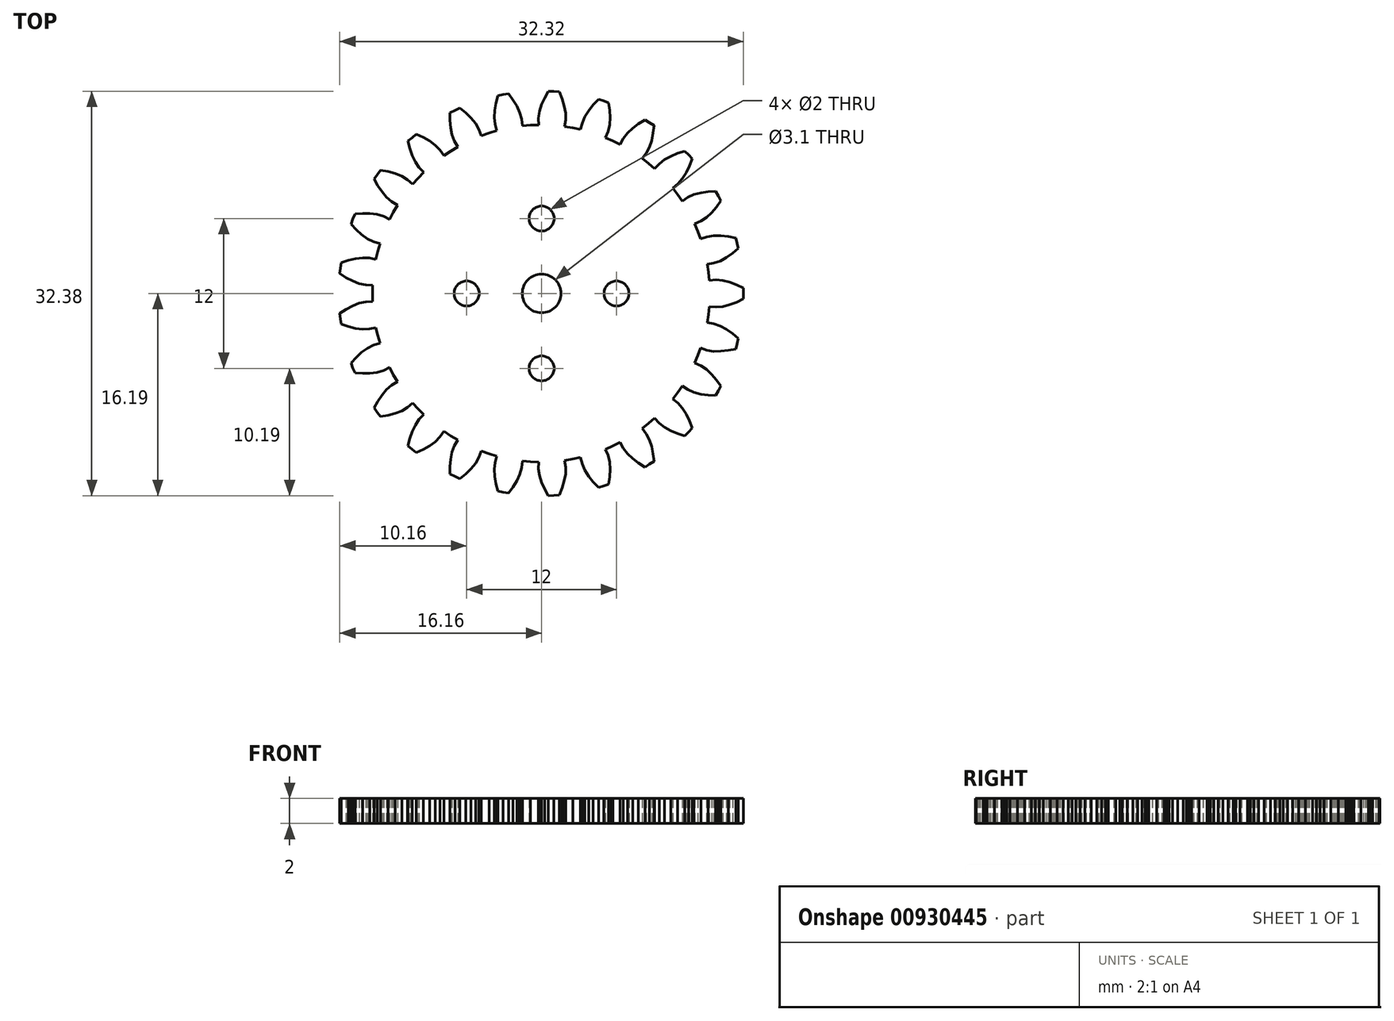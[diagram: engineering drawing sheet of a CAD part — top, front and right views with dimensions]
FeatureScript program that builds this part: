
annotation { "Feature Type Name" : "Feature", "Feature Type Description" : "" }
export const myFeature = defineFeature(function(context is Context, id is Id, definition is map)
    precondition{}
    {
        {
            var Q0;
            Q0=qCreatedBy(makeId("Top.planeOp"),FACE);
            var sketch = newSketch(context, id + "F0", { "sketchPlane" : qUnion([Q0])});
            skLineSegment(sketch, "E0", {"start": v(13.35, -1.7) * mm, "end": v(13.42, -1.05) * mm});
            skLineSegment(sketch, "E1", {"start": v(13.42, -1.05) * mm, "end": v(13.96, -1.1) * mm});
            skLineSegment(sketch, "E2", {"start": v(13.96, -1.1) * mm, "end": v(14.5, -1.05) * mm});
            skLineSegment(sketch, "E3", {"start": v(14.5, -1.05) * mm, "end": v(15.05, -0.9) * mm});
            skLineSegment(sketch, "E4", {"start": v(15.05, -0.9) * mm, "end": v(15.6, -0.7) * mm});
            skLineSegment(sketch, "E5", {"start": v(15.6, -0.7) * mm, "end": v(16.15, -0.43) * mm});
            skLineSegment(sketch, "E6", {"start": v(16.15, -0.43) * mm, "end": v(16.16, 0) * mm});
            skLineSegment(sketch, "E7", {"start": v(16.16, 0) * mm, "end": v(16.15, 0.43) * mm});
            skLineSegment(sketch, "E8", {"start": v(16.15, 0.43) * mm, "end": v(15.6, 0.7) * mm});
            skLineSegment(sketch, "E9", {"start": v(15.6, 0.7) * mm, "end": v(15.05, 0.9) * mm});
            skLineSegment(sketch, "E10", {"start": v(15.05, 0.9) * mm, "end": v(14.5, 1.05) * mm});
            skLineSegment(sketch, "E11", {"start": v(14.5, 1.05) * mm, "end": v(13.96, 1.1) * mm});
            skLineSegment(sketch, "E12", {"start": v(13.96, 1.1) * mm, "end": v(13.42, 1.05) * mm});
            skLineSegment(sketch, "E13", {"start": v(13.42, 1.05) * mm, "end": v(13.35, 1.7) * mm});
            skLineSegment(sketch, "E14", {"start": v(13.35, 1.7) * mm, "end": v(13.26, 2.33) * mm});
            skLineSegment(sketch, "E15", {"start": v(13.26, 2.33) * mm, "end": v(13.79, 2.42) * mm});
            skLineSegment(sketch, "E16", {"start": v(13.79, 2.42) * mm, "end": v(14.3, 2.6) * mm});
            skLineSegment(sketch, "E17", {"start": v(14.3, 2.6) * mm, "end": v(14.8, 2.88) * mm});
            skLineSegment(sketch, "E18", {"start": v(14.8, 2.88) * mm, "end": v(15.29, 3.22) * mm});
            skLineSegment(sketch, "E19", {"start": v(15.29, 3.22) * mm, "end": v(15.75, 3.6) * mm});
            skLineSegment(sketch, "E20", {"start": v(15.75, 3.6) * mm, "end": v(15.65, 4.03) * mm});
            skLineSegment(sketch, "E21", {"start": v(15.65, 4.03) * mm, "end": v(15.54, 4.45) * mm});
            skLineSegment(sketch, "E22", {"start": v(15.54, 4.45) * mm, "end": v(14.94, 4.57) * mm});
            skLineSegment(sketch, "E23", {"start": v(14.94, 4.57) * mm, "end": v(14.35, 4.63) * mm});
            skLineSegment(sketch, "E24", {"start": v(14.35, 4.63) * mm, "end": v(13.79, 4.63) * mm});
            skLineSegment(sketch, "E25", {"start": v(13.79, 4.63) * mm, "end": v(13.25, 4.54) * mm});
            skLineSegment(sketch, "E26", {"start": v(13.25, 4.54) * mm, "end": v(12.74, 4.36) * mm});
            skLineSegment(sketch, "E27", {"start": v(12.74, 4.36) * mm, "end": v(12.51, 4.97) * mm});
            skLineSegment(sketch, "E28", {"start": v(12.51, 4.97) * mm, "end": v(12.26, 5.57) * mm});
            skLineSegment(sketch, "E29", {"start": v(12.26, 5.57) * mm, "end": v(12.75, 5.79) * mm});
            skLineSegment(sketch, "E30", {"start": v(12.75, 5.79) * mm, "end": v(13.2, 6.09) * mm});
            skLineSegment(sketch, "E31", {"start": v(13.2, 6.09) * mm, "end": v(13.62, 6.48) * mm});
            skLineSegment(sketch, "E32", {"start": v(13.62, 6.48) * mm, "end": v(14, 6.93) * mm});
            skLineSegment(sketch, "E33", {"start": v(14, 6.93) * mm, "end": v(14.36, 7.42) * mm});
            skLineSegment(sketch, "E34", {"start": v(14.36, 7.42) * mm, "end": v(14.16, 7.8) * mm});
            skLineSegment(sketch, "E35", {"start": v(14.16, 7.8) * mm, "end": v(13.94, 8.18) * mm});
            skLineSegment(sketch, "E36", {"start": v(13.94, 8.18) * mm, "end": v(13.33, 8.15) * mm});
            skLineSegment(sketch, "E37", {"start": v(13.33, 8.15) * mm, "end": v(12.75, 8.06) * mm});
            skLineSegment(sketch, "E38", {"start": v(12.75, 8.06) * mm, "end": v(12.2, 7.92) * mm});
            skLineSegment(sketch, "E39", {"start": v(12.2, 7.92) * mm, "end": v(11.7, 7.7) * mm});
            skLineSegment(sketch, "E40", {"start": v(11.7, 7.7) * mm, "end": v(11.25, 7.4) * mm});
            skLineSegment(sketch, "E41", {"start": v(11.25, 7.4) * mm, "end": v(10.88, 7.94) * mm});
            skLineSegment(sketch, "E42", {"start": v(10.88, 7.94) * mm, "end": v(10.49, 8.45) * mm});
            skLineSegment(sketch, "E43", {"start": v(10.49, 8.45) * mm, "end": v(10.91, 8.79) * mm});
            skLineSegment(sketch, "E44", {"start": v(10.91, 8.79) * mm, "end": v(11.28, 9.2) * mm});
            skLineSegment(sketch, "E45", {"start": v(11.28, 9.2) * mm, "end": v(11.58, 9.67) * mm});
            skLineSegment(sketch, "E46", {"start": v(11.58, 9.67) * mm, "end": v(11.84, 10.2) * mm});
            skLineSegment(sketch, "E47", {"start": v(11.84, 10.2) * mm, "end": v(12.06, 10.77) * mm});
            skLineSegment(sketch, "E48", {"start": v(12.06, 10.77) * mm, "end": v(11.77, 11.09) * mm});
            skLineSegment(sketch, "E49", {"start": v(11.77, 11.09) * mm, "end": v(11.47, 11.4) * mm});
            skLineSegment(sketch, "E50", {"start": v(11.47, 11.4) * mm, "end": v(10.89, 11.22) * mm});
            skLineSegment(sketch, "E51", {"start": v(10.89, 11.22) * mm, "end": v(10.34, 11) * mm});
            skLineSegment(sketch, "E52", {"start": v(10.34, 11) * mm, "end": v(9.85, 10.72) * mm});
            skLineSegment(sketch, "E53", {"start": v(9.85, 10.72) * mm, "end": v(9.42, 10.38) * mm});
            skLineSegment(sketch, "E54", {"start": v(9.42, 10.38) * mm, "end": v(9.05, 9.98) * mm});
            skLineSegment(sketch, "E55", {"start": v(9.05, 9.98) * mm, "end": v(8.57, 10.4) * mm});
            skLineSegment(sketch, "E56", {"start": v(8.57, 10.4) * mm, "end": v(8.06, 10.8) * mm});
            skLineSegment(sketch, "E57", {"start": v(8.06, 10.8) * mm, "end": v(8.38, 11.23) * mm});
            skLineSegment(sketch, "E58", {"start": v(8.38, 11.23) * mm, "end": v(8.64, 11.72) * mm});
            skLineSegment(sketch, "E59", {"start": v(8.64, 11.72) * mm, "end": v(8.81, 12.26) * mm});
            skLineSegment(sketch, "E60", {"start": v(8.81, 12.26) * mm, "end": v(8.93, 12.84) * mm});
            skLineSegment(sketch, "E61", {"start": v(8.93, 12.84) * mm, "end": v(9, 13.44) * mm});
            skLineSegment(sketch, "E62", {"start": v(9, 13.44) * mm, "end": v(8.64, 13.68) * mm});
            skLineSegment(sketch, "E63", {"start": v(8.64, 13.68) * mm, "end": v(8.27, 13.9) * mm});
            skLineSegment(sketch, "E64", {"start": v(8.27, 13.9) * mm, "end": v(7.76, 13.58) * mm});
            skLineSegment(sketch, "E65", {"start": v(7.76, 13.58) * mm, "end": v(7.28, 13.23) * mm});
            skLineSegment(sketch, "E66", {"start": v(7.28, 13.23) * mm, "end": v(6.87, 12.84) * mm});
            skLineSegment(sketch, "E67", {"start": v(6.87, 12.84) * mm, "end": v(6.54, 12.4) * mm});
            skLineSegment(sketch, "E68", {"start": v(6.54, 12.4) * mm, "end": v(6.29, 11.93) * mm});
            skLineSegment(sketch, "E69", {"start": v(6.29, 11.93) * mm, "end": v(5.7, 12.22) * mm});
            skLineSegment(sketch, "E70", {"start": v(5.7, 12.22) * mm, "end": v(5.12, 12.48) * mm});
            skLineSegment(sketch, "E71", {"start": v(5.12, 12.48) * mm, "end": v(5.32, 12.98) * mm});
            skLineSegment(sketch, "E72", {"start": v(5.32, 12.98) * mm, "end": v(5.45, 13.5) * mm});
            skLineSegment(sketch, "E73", {"start": v(5.45, 13.5) * mm, "end": v(5.48, 14.07) * mm});
            skLineSegment(sketch, "E74", {"start": v(5.48, 14.07) * mm, "end": v(5.46, 14.66) * mm});
            skLineSegment(sketch, "E75", {"start": v(5.46, 14.66) * mm, "end": v(5.38, 15.27) * mm});
            skLineSegment(sketch, "E76", {"start": v(5.38, 15.27) * mm, "end": v(4.97, 15.4) * mm});
            skLineSegment(sketch, "E77", {"start": v(4.97, 15.4) * mm, "end": v(4.55, 15.54) * mm});
            skLineSegment(sketch, "E78", {"start": v(4.55, 15.54) * mm, "end": v(4.13, 15.1) * mm});
            skLineSegment(sketch, "E79", {"start": v(4.13, 15.1) * mm, "end": v(3.76, 14.63) * mm});
            skLineSegment(sketch, "E80", {"start": v(3.76, 14.63) * mm, "end": v(3.46, 14.15) * mm});
            skLineSegment(sketch, "E81", {"start": v(3.46, 14.15) * mm, "end": v(3.25, 13.65) * mm});
            skLineSegment(sketch, "E82", {"start": v(3.25, 13.65) * mm, "end": v(3.12, 13.12) * mm});
            skLineSegment(sketch, "E83", {"start": v(3.12, 13.12) * mm, "end": v(2.49, 13.26) * mm});
            skLineSegment(sketch, "E84", {"start": v(2.49, 13.26) * mm, "end": v(1.85, 13.37) * mm});
            skLineSegment(sketch, "E85", {"start": v(1.85, 13.37) * mm, "end": v(1.93, 13.9) * mm});
            skLineSegment(sketch, "E86", {"start": v(1.93, 13.9) * mm, "end": v(1.92, 14.45) * mm});
            skLineSegment(sketch, "E87", {"start": v(1.92, 14.45) * mm, "end": v(1.81, 15) * mm});
            skLineSegment(sketch, "E88", {"start": v(1.81, 15) * mm, "end": v(1.64, 15.57) * mm});
            skLineSegment(sketch, "E89", {"start": v(1.64, 15.57) * mm, "end": v(1.4, 16.14) * mm});
            skLineSegment(sketch, "E90", {"start": v(1.4, 16.14) * mm, "end": v(0.98, 16.17) * mm});
            skLineSegment(sketch, "E91", {"start": v(0.98, 16.17) * mm, "end": v(0.55, 16.19) * mm});
            skLineSegment(sketch, "E92", {"start": v(0.55, 16.19) * mm, "end": v(0.25, 15.66) * mm});
            skLineSegment(sketch, "E93", {"start": v(0.25, 15.66) * mm, "end": v(0, 15.12) * mm});
            skLineSegment(sketch, "E94", {"start": v(0, 15.12) * mm, "end": v(-0.17, 14.58) * mm});
            skLineSegment(sketch, "E95", {"start": v(-0.17, 14.58) * mm, "end": v(-0.25, 14.04) * mm});
            skLineSegment(sketch, "E96", {"start": v(-0.25, 14.04) * mm, "end": v(-0.24, 13.5) * mm});
            skLineSegment(sketch, "E97", {"start": v(-0.24, 13.5) * mm, "end": v(-0.89, 13.47) * mm});
            skLineSegment(sketch, "E98", {"start": v(-0.89, 13.47) * mm, "end": v(-1.53, 13.42) * mm});
            skLineSegment(sketch, "E99", {"start": v(-1.53, 13.42) * mm, "end": v(-1.6, 13.95) * mm});
            skLineSegment(sketch, "E100", {"start": v(-1.6, 13.95) * mm, "end": v(-1.74, 14.48) * mm});
            skLineSegment(sketch, "E101", {"start": v(-1.74, 14.48) * mm, "end": v(-1.98, 15) * mm});
            skLineSegment(sketch, "E102", {"start": v(-1.98, 15) * mm, "end": v(-2.29, 15.5) * mm});
            skLineSegment(sketch, "E103", {"start": v(-2.29, 15.5) * mm, "end": v(-2.65, 15.99) * mm});
            skLineSegment(sketch, "E104", {"start": v(-2.65, 15.99) * mm, "end": v(-3.08, 15.91) * mm});
            skLineSegment(sketch, "E105", {"start": v(-3.08, 15.91) * mm, "end": v(-3.5, 15.83) * mm});
            skLineSegment(sketch, "E106", {"start": v(-3.5, 15.83) * mm, "end": v(-3.66, 15.24) * mm});
            skLineSegment(sketch, "E107", {"start": v(-3.66, 15.24) * mm, "end": v(-3.76, 14.66) * mm});
            skLineSegment(sketch, "E108", {"start": v(-3.76, 14.66) * mm, "end": v(-3.8, 14.09) * mm});
            skLineSegment(sketch, "E109", {"start": v(-3.8, 14.09) * mm, "end": v(-3.73, 13.55) * mm});
            skLineSegment(sketch, "E110", {"start": v(-3.73, 13.55) * mm, "end": v(-3.6, 13.02) * mm});
            skLineSegment(sketch, "E111", {"start": v(-3.6, 13.02) * mm, "end": v(-4.21, 12.84) * mm});
            skLineSegment(sketch, "E112", {"start": v(-4.21, 12.84) * mm, "end": v(-4.82, 12.62) * mm});
            skLineSegment(sketch, "E113", {"start": v(-4.82, 12.62) * mm, "end": v(-5.01, 13.13) * mm});
            skLineSegment(sketch, "E114", {"start": v(-5.01, 13.13) * mm, "end": v(-5.28, 13.6) * mm});
            skLineSegment(sketch, "E115", {"start": v(-5.28, 13.6) * mm, "end": v(-5.65, 14.04) * mm});
            skLineSegment(sketch, "E116", {"start": v(-5.65, 14.04) * mm, "end": v(-6.07, 14.45) * mm});
            skLineSegment(sketch, "E117", {"start": v(-6.07, 14.45) * mm, "end": v(-6.54, 14.84) * mm});
            skLineSegment(sketch, "E118", {"start": v(-6.54, 14.84) * mm, "end": v(-6.94, 14.66) * mm});
            skLineSegment(sketch, "E119", {"start": v(-6.94, 14.66) * mm, "end": v(-7.33, 14.47) * mm});
            skLineSegment(sketch, "E120", {"start": v(-7.33, 14.47) * mm, "end": v(-7.33, 13.86) * mm});
            skLineSegment(sketch, "E121", {"start": v(-7.33, 13.86) * mm, "end": v(-7.28, 13.27) * mm});
            skLineSegment(sketch, "E122", {"start": v(-7.28, 13.27) * mm, "end": v(-7.18, 12.71) * mm});
            skLineSegment(sketch, "E123", {"start": v(-7.18, 12.71) * mm, "end": v(-6.99, 12.2) * mm});
            skLineSegment(sketch, "E124", {"start": v(-6.99, 12.2) * mm, "end": v(-6.72, 11.73) * mm});
            skLineSegment(sketch, "E125", {"start": v(-6.72, 11.73) * mm, "end": v(-7.27, 11.4) * mm});
            skLineSegment(sketch, "E126", {"start": v(-7.27, 11.4) * mm, "end": v(-7.81, 11.04) * mm});
            skLineSegment(sketch, "E127", {"start": v(-7.81, 11.04) * mm, "end": v(-8.12, 11.48) * mm});
            skLineSegment(sketch, "E128", {"start": v(-8.12, 11.48) * mm, "end": v(-8.5, 11.87) * mm});
            skLineSegment(sketch, "E129", {"start": v(-8.5, 11.87) * mm, "end": v(-8.96, 12.2) * mm});
            skLineSegment(sketch, "E130", {"start": v(-8.96, 12.2) * mm, "end": v(-9.48, 12.5) * mm});
            skLineSegment(sketch, "E131", {"start": v(-9.48, 12.5) * mm, "end": v(-10.03, 12.75) * mm});
            skLineSegment(sketch, "E132", {"start": v(-10.03, 12.75) * mm, "end": v(-10.37, 12.48) * mm});
            skLineSegment(sketch, "E133", {"start": v(-10.37, 12.48) * mm, "end": v(-10.7, 12.2) * mm});
            skLineSegment(sketch, "E134", {"start": v(-10.7, 12.2) * mm, "end": v(-10.55, 11.61) * mm});
            skLineSegment(sketch, "E135", {"start": v(-10.55, 11.61) * mm, "end": v(-10.36, 11.05) * mm});
            skLineSegment(sketch, "E136", {"start": v(-10.36, 11.05) * mm, "end": v(-10.12, 10.54) * mm});
            skLineSegment(sketch, "E137", {"start": v(-10.12, 10.54) * mm, "end": v(-9.8, 10.1) * mm});
            skLineSegment(sketch, "E138", {"start": v(-9.8, 10.1) * mm, "end": v(-9.43, 9.7) * mm});
            skLineSegment(sketch, "E139", {"start": v(-9.43, 9.7) * mm, "end": v(-9.88, 9.24) * mm});
            skLineSegment(sketch, "E140", {"start": v(-9.88, 9.24) * mm, "end": v(-10.31, 8.76) * mm});
            skLineSegment(sketch, "E141", {"start": v(-10.31, 8.76) * mm, "end": v(-10.72, 9.1) * mm});
            skLineSegment(sketch, "E142", {"start": v(-10.72, 9.1) * mm, "end": v(-11.19, 9.4) * mm});
            skLineSegment(sketch, "E143", {"start": v(-11.19, 9.4) * mm, "end": v(-11.72, 9.6) * mm});
            skLineSegment(sketch, "E144", {"start": v(-11.72, 9.6) * mm, "end": v(-12.29, 9.76) * mm});
            skLineSegment(sketch, "E145", {"start": v(-12.29, 9.76) * mm, "end": v(-12.89, 9.87) * mm});
            skLineSegment(sketch, "E146", {"start": v(-12.89, 9.87) * mm, "end": v(-13.15, 9.52) * mm});
            skLineSegment(sketch, "E147", {"start": v(-13.15, 9.52) * mm, "end": v(-13.4, 9.17) * mm});
            skLineSegment(sketch, "E148", {"start": v(-13.4, 9.17) * mm, "end": v(-13.1, 8.63) * mm});
            skLineSegment(sketch, "E149", {"start": v(-13.1, 8.63) * mm, "end": v(-12.78, 8.14) * mm});
            skLineSegment(sketch, "E150", {"start": v(-12.78, 8.14) * mm, "end": v(-12.42, 7.7) * mm});
            skLineSegment(sketch, "E151", {"start": v(-12.42, 7.7) * mm, "end": v(-12, 7.35) * mm});
            skLineSegment(sketch, "E152", {"start": v(-12, 7.35) * mm, "end": v(-11.54, 7.06) * mm});
            skLineSegment(sketch, "E153", {"start": v(-11.54, 7.06) * mm, "end": v(-11.87, 6.5) * mm});
            skLineSegment(sketch, "E154", {"start": v(-11.87, 6.5) * mm, "end": v(-12.17, 5.93) * mm});
            skLineSegment(sketch, "E155", {"start": v(-12.17, 5.93) * mm, "end": v(-12.65, 6.17) * mm});
            skLineSegment(sketch, "E156", {"start": v(-12.65, 6.17) * mm, "end": v(-13.18, 6.33) * mm});
            skLineSegment(sketch, "E157", {"start": v(-13.18, 6.33) * mm, "end": v(-13.74, 6.4) * mm});
            skLineSegment(sketch, "E158", {"start": v(-13.74, 6.4) * mm, "end": v(-14.33, 6.4) * mm});
            skLineSegment(sketch, "E159", {"start": v(-14.33, 6.4) * mm, "end": v(-14.94, 6.36) * mm});
            skLineSegment(sketch, "E160", {"start": v(-14.94, 6.36) * mm, "end": v(-15.1, 5.96) * mm});
            skLineSegment(sketch, "E161", {"start": v(-15.1, 5.96) * mm, "end": v(-15.26, 5.56) * mm});
            skLineSegment(sketch, "E162", {"start": v(-15.26, 5.56) * mm, "end": v(-14.84, 5.11) * mm});
            skLineSegment(sketch, "E163", {"start": v(-14.84, 5.11) * mm, "end": v(-14.4, 4.72) * mm});
            skLineSegment(sketch, "E164", {"start": v(-14.4, 4.72) * mm, "end": v(-13.95, 4.38) * mm});
            skLineSegment(sketch, "E165", {"start": v(-13.95, 4.38) * mm, "end": v(-13.46, 4.14) * mm});
            skLineSegment(sketch, "E166", {"start": v(-13.46, 4.14) * mm, "end": v(-12.94, 3.98) * mm});
            skLineSegment(sketch, "E167", {"start": v(-12.94, 3.98) * mm, "end": v(-13.12, 3.36) * mm});
            skLineSegment(sketch, "E168", {"start": v(-13.12, 3.36) * mm, "end": v(-13.26, 2.73) * mm});
            skLineSegment(sketch, "E169", {"start": v(-13.26, 2.73) * mm, "end": v(-13.8, 2.84) * mm});
            skLineSegment(sketch, "E170", {"start": v(-13.8, 2.84) * mm, "end": v(-14.34, 2.86) * mm});
            skLineSegment(sketch, "E171", {"start": v(-14.34, 2.86) * mm, "end": v(-14.9, 2.79) * mm});
            skLineSegment(sketch, "E172", {"start": v(-14.9, 2.79) * mm, "end": v(-15.47, 2.65) * mm});
            skLineSegment(sketch, "E173", {"start": v(-15.47, 2.65) * mm, "end": v(-16.05, 2.46) * mm});
            skLineSegment(sketch, "E174", {"start": v(-16.05, 2.46) * mm, "end": v(-16.11, 2.03) * mm});
            skLineSegment(sketch, "E175", {"start": v(-16.11, 2.03) * mm, "end": v(-16.16, 1.6) * mm});
            skLineSegment(sketch, "E176", {"start": v(-16.16, 1.6) * mm, "end": v(-15.65, 1.27) * mm});
            skLineSegment(sketch, "E177", {"start": v(-15.65, 1.27) * mm, "end": v(-15.13, 1) * mm});
            skLineSegment(sketch, "E178", {"start": v(-15.13, 1) * mm, "end": v(-14.6, 0.78) * mm});
            skLineSegment(sketch, "E179", {"start": v(-14.6, 0.78) * mm, "end": v(-14.06, 0.67) * mm});
            skLineSegment(sketch, "E180", {"start": v(-14.06, 0.67) * mm, "end": v(-13.52, 0.65) * mm});
            skLineSegment(sketch, "E181", {"start": v(-13.52, 0.65) * mm, "end": v(-13.54, 0) * mm});
            skLineSegment(sketch, "E182", {"start": v(-13.54, 0) * mm, "end": v(-13.52, -0.65) * mm});
            skLineSegment(sketch, "E183", {"start": v(-13.52, -0.65) * mm, "end": v(-14.06, -0.67) * mm});
            skLineSegment(sketch, "E184", {"start": v(-14.06, -0.67) * mm, "end": v(-14.6, -0.78) * mm});
            skLineSegment(sketch, "E185", {"start": v(-14.6, -0.78) * mm, "end": v(-15.13, -1) * mm});
            skLineSegment(sketch, "E186", {"start": v(-15.13, -1) * mm, "end": v(-15.65, -1.27) * mm});
            skLineSegment(sketch, "E187", {"start": v(-15.65, -1.27) * mm, "end": v(-16.16, -1.6) * mm});
            skLineSegment(sketch, "E188", {"start": v(-16.16, -1.6) * mm, "end": v(-16.11, -2.03) * mm});
            skLineSegment(sketch, "E189", {"start": v(-16.11, -2.03) * mm, "end": v(-16.05, -2.46) * mm});
            skLineSegment(sketch, "E190", {"start": v(-16.05, -2.46) * mm, "end": v(-15.47, -2.65) * mm});
            skLineSegment(sketch, "E191", {"start": v(-15.47, -2.65) * mm, "end": v(-14.9, -2.79) * mm});
            skLineSegment(sketch, "E192", {"start": v(-14.9, -2.79) * mm, "end": v(-14.34, -2.86) * mm});
            skLineSegment(sketch, "E193", {"start": v(-14.34, -2.86) * mm, "end": v(-13.8, -2.84) * mm});
            skLineSegment(sketch, "E194", {"start": v(-13.8, -2.84) * mm, "end": v(-13.26, -2.73) * mm});
            skLineSegment(sketch, "E195", {"start": v(-13.26, -2.73) * mm, "end": v(-13.12, -3.36) * mm});
            skLineSegment(sketch, "E196", {"start": v(-13.12, -3.36) * mm, "end": v(-12.94, -3.98) * mm});
            skLineSegment(sketch, "E197", {"start": v(-12.94, -3.98) * mm, "end": v(-13.46, -4.14) * mm});
            skLineSegment(sketch, "E198", {"start": v(-13.46, -4.14) * mm, "end": v(-13.95, -4.38) * mm});
            skLineSegment(sketch, "E199", {"start": v(-13.95, -4.38) * mm, "end": v(-14.4, -4.72) * mm});
            skLineSegment(sketch, "E200", {"start": v(-14.4, -4.72) * mm, "end": v(-14.84, -5.11) * mm});
            skLineSegment(sketch, "E201", {"start": v(-14.84, -5.11) * mm, "end": v(-15.26, -5.56) * mm});
            skLineSegment(sketch, "E202", {"start": v(-15.26, -5.56) * mm, "end": v(-15.1, -5.96) * mm});
            skLineSegment(sketch, "E203", {"start": v(-15.1, -5.96) * mm, "end": v(-14.94, -6.36) * mm});
            skLineSegment(sketch, "E204", {"start": v(-14.94, -6.36) * mm, "end": v(-14.33, -6.4) * mm});
            skLineSegment(sketch, "E205", {"start": v(-14.33, -6.4) * mm, "end": v(-13.74, -6.4) * mm});
            skLineSegment(sketch, "E206", {"start": v(-13.74, -6.4) * mm, "end": v(-13.18, -6.33) * mm});
            skLineSegment(sketch, "E207", {"start": v(-13.18, -6.33) * mm, "end": v(-12.65, -6.17) * mm});
            skLineSegment(sketch, "E208", {"start": v(-12.65, -6.17) * mm, "end": v(-12.17, -5.93) * mm});
            skLineSegment(sketch, "E209", {"start": v(-12.17, -5.93) * mm, "end": v(-11.87, -6.5) * mm});
            skLineSegment(sketch, "E210", {"start": v(-11.87, -6.5) * mm, "end": v(-11.54, -7.06) * mm});
            skLineSegment(sketch, "E211", {"start": v(-11.54, -7.06) * mm, "end": v(-12, -7.35) * mm});
            skLineSegment(sketch, "E212", {"start": v(-12, -7.35) * mm, "end": v(-12.42, -7.7) * mm});
            skLineSegment(sketch, "E213", {"start": v(-12.42, -7.7) * mm, "end": v(-12.78, -8.14) * mm});
            skLineSegment(sketch, "E214", {"start": v(-12.78, -8.14) * mm, "end": v(-13.1, -8.63) * mm});
            skLineSegment(sketch, "E215", {"start": v(-13.1, -8.63) * mm, "end": v(-13.4, -9.17) * mm});
            skLineSegment(sketch, "E216", {"start": v(-13.4, -9.17) * mm, "end": v(-13.15, -9.52) * mm});
            skLineSegment(sketch, "E217", {"start": v(-13.15, -9.52) * mm, "end": v(-12.89, -9.87) * mm});
            skLineSegment(sketch, "E218", {"start": v(-12.89, -9.87) * mm, "end": v(-12.29, -9.76) * mm});
            skLineSegment(sketch, "E219", {"start": v(-12.29, -9.76) * mm, "end": v(-11.72, -9.6) * mm});
            skLineSegment(sketch, "E220", {"start": v(-11.72, -9.6) * mm, "end": v(-11.19, -9.4) * mm});
            skLineSegment(sketch, "E221", {"start": v(-11.19, -9.4) * mm, "end": v(-10.72, -9.1) * mm});
            skLineSegment(sketch, "E222", {"start": v(-10.72, -9.1) * mm, "end": v(-10.31, -8.76) * mm});
            skLineSegment(sketch, "E223", {"start": v(-10.31, -8.76) * mm, "end": v(-9.88, -9.24) * mm});
            skLineSegment(sketch, "E224", {"start": v(-9.88, -9.24) * mm, "end": v(-9.43, -9.7) * mm});
            skLineSegment(sketch, "E225", {"start": v(-9.43, -9.7) * mm, "end": v(-9.8, -10.1) * mm});
            skLineSegment(sketch, "E226", {"start": v(-9.8, -10.1) * mm, "end": v(-10.12, -10.54) * mm});
            skLineSegment(sketch, "E227", {"start": v(-10.12, -10.54) * mm, "end": v(-10.36, -11.05) * mm});
            skLineSegment(sketch, "E228", {"start": v(-10.36, -11.05) * mm, "end": v(-10.55, -11.61) * mm});
            skLineSegment(sketch, "E229", {"start": v(-10.55, -11.61) * mm, "end": v(-10.7, -12.2) * mm});
            skLineSegment(sketch, "E230", {"start": v(-10.7, -12.2) * mm, "end": v(-10.37, -12.48) * mm});
            skLineSegment(sketch, "E231", {"start": v(-10.37, -12.48) * mm, "end": v(-10.03, -12.75) * mm});
            skLineSegment(sketch, "E232", {"start": v(-10.03, -12.75) * mm, "end": v(-9.48, -12.5) * mm});
            skLineSegment(sketch, "E233", {"start": v(-9.48, -12.5) * mm, "end": v(-8.96, -12.2) * mm});
            skLineSegment(sketch, "E234", {"start": v(-8.96, -12.2) * mm, "end": v(-8.5, -11.87) * mm});
            skLineSegment(sketch, "E235", {"start": v(-8.5, -11.87) * mm, "end": v(-8.12, -11.48) * mm});
            skLineSegment(sketch, "E236", {"start": v(-8.12, -11.48) * mm, "end": v(-7.81, -11.04) * mm});
            skLineSegment(sketch, "E237", {"start": v(-7.81, -11.04) * mm, "end": v(-7.27, -11.4) * mm});
            skLineSegment(sketch, "E238", {"start": v(-7.27, -11.4) * mm, "end": v(-6.72, -11.73) * mm});
            skLineSegment(sketch, "E239", {"start": v(-6.72, -11.73) * mm, "end": v(-6.99, -12.2) * mm});
            skLineSegment(sketch, "E240", {"start": v(-6.99, -12.2) * mm, "end": v(-7.18, -12.71) * mm});
            skLineSegment(sketch, "E241", {"start": v(-7.18, -12.71) * mm, "end": v(-7.28, -13.27) * mm});
            skLineSegment(sketch, "E242", {"start": v(-7.28, -13.27) * mm, "end": v(-7.33, -13.86) * mm});
            skLineSegment(sketch, "E243", {"start": v(-7.33, -13.86) * mm, "end": v(-7.33, -14.47) * mm});
            skLineSegment(sketch, "E244", {"start": v(-7.33, -14.47) * mm, "end": v(-6.94, -14.66) * mm});
            skLineSegment(sketch, "E245", {"start": v(-6.94, -14.66) * mm, "end": v(-6.54, -14.84) * mm});
            skLineSegment(sketch, "E246", {"start": v(-6.54, -14.84) * mm, "end": v(-6.07, -14.45) * mm});
            skLineSegment(sketch, "E247", {"start": v(-6.07, -14.45) * mm, "end": v(-5.65, -14.04) * mm});
            skLineSegment(sketch, "E248", {"start": v(-5.65, -14.04) * mm, "end": v(-5.28, -13.6) * mm});
            skLineSegment(sketch, "E249", {"start": v(-5.28, -13.6) * mm, "end": v(-5.01, -13.13) * mm});
            skLineSegment(sketch, "E250", {"start": v(-5.01, -13.13) * mm, "end": v(-4.82, -12.62) * mm});
            skLineSegment(sketch, "E251", {"start": v(-4.82, -12.62) * mm, "end": v(-4.21, -12.84) * mm});
            skLineSegment(sketch, "E252", {"start": v(-4.21, -12.84) * mm, "end": v(-3.6, -13.02) * mm});
            skLineSegment(sketch, "E253", {"start": v(-3.6, -13.02) * mm, "end": v(-3.73, -13.55) * mm});
            skLineSegment(sketch, "E254", {"start": v(-3.73, -13.55) * mm, "end": v(-3.8, -14.09) * mm});
            skLineSegment(sketch, "E255", {"start": v(-3.8, -14.09) * mm, "end": v(-3.76, -14.66) * mm});
            skLineSegment(sketch, "E256", {"start": v(-3.76, -14.66) * mm, "end": v(-3.66, -15.24) * mm});
            skLineSegment(sketch, "E257", {"start": v(-3.66, -15.24) * mm, "end": v(-3.5, -15.83) * mm});
            skLineSegment(sketch, "E258", {"start": v(-3.5, -15.83) * mm, "end": v(-3.08, -15.91) * mm});
            skLineSegment(sketch, "E259", {"start": v(-3.08, -15.91) * mm, "end": v(-2.65, -15.99) * mm});
            skLineSegment(sketch, "E260", {"start": v(-2.65, -15.99) * mm, "end": v(-2.29, -15.5) * mm});
            skLineSegment(sketch, "E261", {"start": v(-2.29, -15.5) * mm, "end": v(-1.98, -15) * mm});
            skLineSegment(sketch, "E262", {"start": v(-1.98, -15) * mm, "end": v(-1.74, -14.48) * mm});
            skLineSegment(sketch, "E263", {"start": v(-1.74, -14.48) * mm, "end": v(-1.6, -13.95) * mm});
            skLineSegment(sketch, "E264", {"start": v(-1.6, -13.95) * mm, "end": v(-1.53, -13.42) * mm});
            skLineSegment(sketch, "E265", {"start": v(-1.53, -13.42) * mm, "end": v(-0.89, -13.47) * mm});
            skLineSegment(sketch, "E266", {"start": v(-0.89, -13.47) * mm, "end": v(-0.24, -13.5) * mm});
            skLineSegment(sketch, "E267", {"start": v(-0.24, -13.5) * mm, "end": v(-0.25, -14.04) * mm});
            skLineSegment(sketch, "E268", {"start": v(-0.25, -14.04) * mm, "end": v(-0.17, -14.58) * mm});
            skLineSegment(sketch, "E269", {"start": v(-0.17, -14.58) * mm, "end": v(0, -15.12) * mm});
            skLineSegment(sketch, "E270", {"start": v(0, -15.12) * mm, "end": v(0.25, -15.66) * mm});
            skLineSegment(sketch, "E271", {"start": v(0.25, -15.66) * mm, "end": v(0.55, -16.19) * mm});
            skLineSegment(sketch, "E272", {"start": v(0.55, -16.19) * mm, "end": v(0.98, -16.17) * mm});
            skLineSegment(sketch, "E273", {"start": v(0.98, -16.17) * mm, "end": v(1.4, -16.14) * mm});
            skLineSegment(sketch, "E274", {"start": v(1.4, -16.14) * mm, "end": v(1.64, -15.57) * mm});
            skLineSegment(sketch, "E275", {"start": v(1.64, -15.57) * mm, "end": v(1.81, -15) * mm});
            skLineSegment(sketch, "E276", {"start": v(1.81, -15) * mm, "end": v(1.92, -14.45) * mm});
            skLineSegment(sketch, "E277", {"start": v(1.92, -14.45) * mm, "end": v(1.93, -13.9) * mm});
            skLineSegment(sketch, "E278", {"start": v(1.93, -13.9) * mm, "end": v(1.85, -13.37) * mm});
            skLineSegment(sketch, "E279", {"start": v(1.85, -13.37) * mm, "end": v(2.49, -13.26) * mm});
            skLineSegment(sketch, "E280", {"start": v(2.49, -13.26) * mm, "end": v(3.12, -13.12) * mm});
            skLineSegment(sketch, "E281", {"start": v(3.12, -13.12) * mm, "end": v(3.25, -13.65) * mm});
            skLineSegment(sketch, "E282", {"start": v(3.25, -13.65) * mm, "end": v(3.46, -14.15) * mm});
            skLineSegment(sketch, "E283", {"start": v(3.46, -14.15) * mm, "end": v(3.76, -14.63) * mm});
            skLineSegment(sketch, "E284", {"start": v(3.76, -14.63) * mm, "end": v(4.13, -15.1) * mm});
            skLineSegment(sketch, "E285", {"start": v(4.13, -15.1) * mm, "end": v(4.55, -15.54) * mm});
            skLineSegment(sketch, "E286", {"start": v(4.55, -15.54) * mm, "end": v(4.97, -15.4) * mm});
            skLineSegment(sketch, "E287", {"start": v(4.97, -15.4) * mm, "end": v(5.38, -15.27) * mm});
            skLineSegment(sketch, "E288", {"start": v(5.38, -15.27) * mm, "end": v(5.46, -14.66) * mm});
            skLineSegment(sketch, "E289", {"start": v(5.46, -14.66) * mm, "end": v(5.48, -14.07) * mm});
            skLineSegment(sketch, "E290", {"start": v(5.48, -14.07) * mm, "end": v(5.45, -13.5) * mm});
            skLineSegment(sketch, "E291", {"start": v(5.45, -13.5) * mm, "end": v(5.32, -12.98) * mm});
            skLineSegment(sketch, "E292", {"start": v(5.32, -12.98) * mm, "end": v(5.12, -12.48) * mm});
            skLineSegment(sketch, "E293", {"start": v(5.12, -12.48) * mm, "end": v(5.7, -12.22) * mm});
            skLineSegment(sketch, "E294", {"start": v(5.7, -12.22) * mm, "end": v(6.29, -11.93) * mm});
            skLineSegment(sketch, "E295", {"start": v(6.29, -11.93) * mm, "end": v(6.54, -12.4) * mm});
            skLineSegment(sketch, "E296", {"start": v(6.54, -12.4) * mm, "end": v(6.87, -12.84) * mm});
            skLineSegment(sketch, "E297", {"start": v(6.87, -12.84) * mm, "end": v(7.28, -13.23) * mm});
            skLineSegment(sketch, "E298", {"start": v(7.28, -13.23) * mm, "end": v(7.76, -13.58) * mm});
            skLineSegment(sketch, "E299", {"start": v(7.76, -13.58) * mm, "end": v(8.27, -13.9) * mm});
            skLineSegment(sketch, "E300", {"start": v(8.27, -13.9) * mm, "end": v(8.64, -13.68) * mm});
            skLineSegment(sketch, "E301", {"start": v(8.64, -13.68) * mm, "end": v(9, -13.44) * mm});
            skLineSegment(sketch, "E302", {"start": v(9, -13.44) * mm, "end": v(8.93, -12.84) * mm});
            skLineSegment(sketch, "E303", {"start": v(8.93, -12.84) * mm, "end": v(8.81, -12.26) * mm});
            skLineSegment(sketch, "E304", {"start": v(8.81, -12.26) * mm, "end": v(8.64, -11.72) * mm});
            skLineSegment(sketch, "E305", {"start": v(8.64, -11.72) * mm, "end": v(8.38, -11.23) * mm});
            skLineSegment(sketch, "E306", {"start": v(8.38, -11.23) * mm, "end": v(8.06, -10.8) * mm});
            skLineSegment(sketch, "E307", {"start": v(8.06, -10.8) * mm, "end": v(8.57, -10.4) * mm});
            skLineSegment(sketch, "E308", {"start": v(8.57, -10.4) * mm, "end": v(9.05, -9.98) * mm});
            skLineSegment(sketch, "E309", {"start": v(9.05, -9.98) * mm, "end": v(9.42, -10.38) * mm});
            skLineSegment(sketch, "E310", {"start": v(9.42, -10.38) * mm, "end": v(9.85, -10.72) * mm});
            skLineSegment(sketch, "E311", {"start": v(9.85, -10.72) * mm, "end": v(10.34, -11) * mm});
            skLineSegment(sketch, "E312", {"start": v(10.34, -11) * mm, "end": v(10.89, -11.22) * mm});
            skLineSegment(sketch, "E313", {"start": v(10.89, -11.22) * mm, "end": v(11.47, -11.4) * mm});
            skLineSegment(sketch, "E314", {"start": v(11.47, -11.4) * mm, "end": v(11.77, -11.09) * mm});
            skLineSegment(sketch, "E315", {"start": v(11.77, -11.09) * mm, "end": v(12.06, -10.77) * mm});
            skLineSegment(sketch, "E316", {"start": v(12.06, -10.77) * mm, "end": v(11.84, -10.2) * mm});
            skLineSegment(sketch, "E317", {"start": v(11.84, -10.2) * mm, "end": v(11.58, -9.67) * mm});
            skLineSegment(sketch, "E318", {"start": v(11.58, -9.67) * mm, "end": v(11.28, -9.2) * mm});
            skLineSegment(sketch, "E319", {"start": v(11.28, -9.2) * mm, "end": v(10.91, -8.79) * mm});
            skLineSegment(sketch, "E320", {"start": v(10.91, -8.79) * mm, "end": v(10.49, -8.45) * mm});
            skLineSegment(sketch, "E321", {"start": v(10.49, -8.45) * mm, "end": v(10.88, -7.94) * mm});
            skLineSegment(sketch, "E322", {"start": v(10.88, -7.94) * mm, "end": v(11.25, -7.4) * mm});
            skLineSegment(sketch, "E323", {"start": v(11.25, -7.4) * mm, "end": v(11.7, -7.7) * mm});
            skLineSegment(sketch, "E324", {"start": v(11.7, -7.7) * mm, "end": v(12.2, -7.92) * mm});
            skLineSegment(sketch, "E325", {"start": v(12.2, -7.92) * mm, "end": v(12.75, -8.06) * mm});
            skLineSegment(sketch, "E326", {"start": v(12.75, -8.06) * mm, "end": v(13.33, -8.15) * mm});
            skLineSegment(sketch, "E327", {"start": v(13.33, -8.15) * mm, "end": v(13.94, -8.18) * mm});
            skLineSegment(sketch, "E328", {"start": v(13.94, -8.18) * mm, "end": v(14.16, -7.8) * mm});
            skLineSegment(sketch, "E329", {"start": v(14.16, -7.8) * mm, "end": v(14.36, -7.42) * mm});
            skLineSegment(sketch, "E330", {"start": v(14.36, -7.42) * mm, "end": v(14, -6.93) * mm});
            skLineSegment(sketch, "E331", {"start": v(14, -6.93) * mm, "end": v(13.62, -6.48) * mm});
            skLineSegment(sketch, "E332", {"start": v(13.62, -6.48) * mm, "end": v(13.2, -6.09) * mm});
            skLineSegment(sketch, "E333", {"start": v(13.2, -6.09) * mm, "end": v(12.75, -5.79) * mm});
            skLineSegment(sketch, "E334", {"start": v(12.75, -5.79) * mm, "end": v(12.26, -5.57) * mm});
            skLineSegment(sketch, "E335", {"start": v(12.26, -5.57) * mm, "end": v(12.51, -4.97) * mm});
            skLineSegment(sketch, "E336", {"start": v(12.51, -4.97) * mm, "end": v(12.74, -4.36) * mm});
            skLineSegment(sketch, "E337", {"start": v(12.74, -4.36) * mm, "end": v(13.25, -4.54) * mm});
            skLineSegment(sketch, "E338", {"start": v(13.25, -4.54) * mm, "end": v(13.79, -4.63) * mm});
            skLineSegment(sketch, "E339", {"start": v(13.79, -4.63) * mm, "end": v(14.35, -4.63) * mm});
            skLineSegment(sketch, "E340", {"start": v(14.35, -4.63) * mm, "end": v(14.94, -4.57) * mm});
            skLineSegment(sketch, "E341", {"start": v(14.94, -4.57) * mm, "end": v(15.54, -4.45) * mm});
            skLineSegment(sketch, "E342", {"start": v(15.54, -4.45) * mm, "end": v(15.65, -4.03) * mm});
            skLineSegment(sketch, "E343", {"start": v(15.65, -4.03) * mm, "end": v(15.75, -3.6) * mm});
            skLineSegment(sketch, "E344", {"start": v(15.75, -3.6) * mm, "end": v(15.29, -3.22) * mm});
            skLineSegment(sketch, "E345", {"start": v(15.29, -3.22) * mm, "end": v(14.8, -2.88) * mm});
            skLineSegment(sketch, "E346", {"start": v(14.8, -2.88) * mm, "end": v(14.3, -2.6) * mm});
            skLineSegment(sketch, "E347", {"start": v(14.3, -2.6) * mm, "end": v(13.79, -2.42) * mm});
            skLineSegment(sketch, "E348", {"start": v(13.79, -2.42) * mm, "end": v(13.26, -2.33) * mm});
            skLineSegment(sketch, "E349", {"start": v(13.35, -1.7) * mm, "end": v(13.26, -2.33) * mm});
            skSolve(sketch);
        }
        {
            var Q0;
            Q0=qCreatedBy(makeId("Top.planeOp"),FACE);
            cPlane(context, id + "F1", {"entities" : qUnion([Q0]), "cplaneType" : CPlaneType.OFFSET, "offset" : 25 * mm, "width" : 150 * mm, "height" : 150 * mm});
        }
        {
            var Q0;
            Q0=makeQuery(id+"F0.imprint","IMPRINT",FACE,{"disambiguationData":[TD([[makeQuery(id+"F0.imprint","IMPRINT",EDGE,{"derivedFrom":sQuery(id+"F0.wireOp",EDGE,"E0")}),1.0]])]});
            var sketch = newSketch(context, id + "F2", { "sketchPlane" : qUnion([Q0])});
            skCircle(sketch, "E350", {"center": v(0, 0) * mm, "radius": 1.55 * mm});
            skCircle(sketch, "E351", {"center": v(0, 6) * mm, "radius": 1 * mm});
            skCircle(sketch, "E352.1.0", {"center": v(-6, 0) * mm, "radius": 1 * mm});
            skCircle(sketch, "E352.2.0", {"center": v(0, -6) * mm, "radius": 1 * mm});
            skCircle(sketch, "E352.3.0", {"center": v(6, 0) * mm, "radius": 1 * mm});
            skSolve(sketch);
        }
        {
            var Q0;
            Q0=makeQuery(id+"F2.imprint","IMPRINT",FACE,{"disambiguationData":[TD([[makeQuery(id+"F2.imprint","IMPRINT",EDGE,{"derivedFrom":sQuery(id+"F2.wireOp",EDGE,"E350")}),-1.0]])]});
            extrude(context, id + "F3", {"entities" : qUnion([Q0]), "depth" : 2 * mm, "offsetDistance" : 25 * mm});
        }
    });
